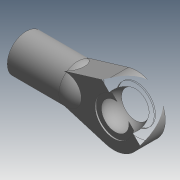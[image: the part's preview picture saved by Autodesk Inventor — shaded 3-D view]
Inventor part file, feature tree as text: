
AUTODESK INVENTOR PART (.ipt)
format: ipt  version: 2014 SP1 (Build 180222100, 222)  size: 136,704 bytes
history: native  units: in
note: dims shown in document units (in); Inventor stores cm internally (conversion verified against a paired STEP export)
features: sketch x6, extrude x5, revolve x1, fillet x1, boolean_combine x1
ambient origin geometry x8: Origin, YZ Plane, XZ Plane, XY Plane, X Axis, Y Axis, Z Axis, Center Point
bodies: Solid1 (feature_tree), Solid2 (feature_tree)
feature tree (14):
  sketch  "Sketch1"  dims[d0=0.4193in d2=0.2756in]
  extrude  "Extrusion1"  Depth=0.2756in
  extrude  "Extrusion2"  Depth=0.1673in
  revolve  "Revolution1"  [1 undecoded]
  extrude  "Extrusion3"  Depth=0.2756in
  extrude  "Extrusion4"  Depth=0.2096in TaperAngle=0.0deg
  fillet  "Fillet1"  Radius=0.1378in
  boolean_combine  "Combine1"
  extrude  "Extrusion5"  Depth=0.3937in TaperAngle=0.0deg
  sketch  "Sketch2"  dims[d3=0.1673in d4=0.0in d5=0.2756in]
  sketch  "Sketch3"  dims[d6=0.1476in d7=0.0in d8=0.25in]
  sketch  "Sketch4"  dims[d9=360.0deg d10=0.2756in]
  sketch  "Sketch5"  dims[d11=0.3937in d12=0.0in d13=0.2096in d14=0.0in d15=0.1378in]
  sketch  "Sketch6"  dims[d16=0.1299in d17=0.3937in d18=0.0in d19=0.7254in]
note: 1 required parameter value undecoded (feature->parameter linkage not recoverable at this tier; creation-order binding heuristic only, values carry confidence <= 0.55)
